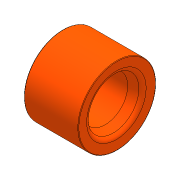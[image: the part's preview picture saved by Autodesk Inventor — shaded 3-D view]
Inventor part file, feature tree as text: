
AUTODESK INVENTOR PART (.ipt)
format: ipt  version: 2017 (Build 210142000, 142)  size: 241,152 bytes
history: native  units: mm
features: fillet x5, revolve x1, sketch x1
ambient origin geometry x8: Origin, YZ Plane, XZ Plane, XY Plane, X Axis, Y Axis, Z Axis, Center Point
bodies: Solid1 (feature_tree)
feature tree (7):
  revolve  "Revolution1"  [1 undecoded]
  fillet  "Fillet8"  Radius=69.5mm
  fillet  "Fillet9"  Radius=63.0mm
  fillet  "Fillet10"  Radius=7.0mm
  fillet  "Fillet11"  Radius=7.0mm
  fillet  "Fillet12"  Radius=6.0mm
  sketch  "Sketch1"  dims[d2=90.0deg d27=46.5mm d29=69.5mm d31=63.0mm d32=7.0mm d33=7.0mm d34=6.0mm d35=55.0mm d39=80.0mm d40=1.4mm d42=5.6mm d44=19.0mm d45=19.0mm d46=56.0mm d47=0.872665mm d48=0.872665mm d49=12.5mm d50=5.0mm d54=0.5mm]
note: 1 required parameter value undecoded (feature->parameter linkage not recoverable at this tier; creation-order binding heuristic only, values carry confidence <= 0.55)
